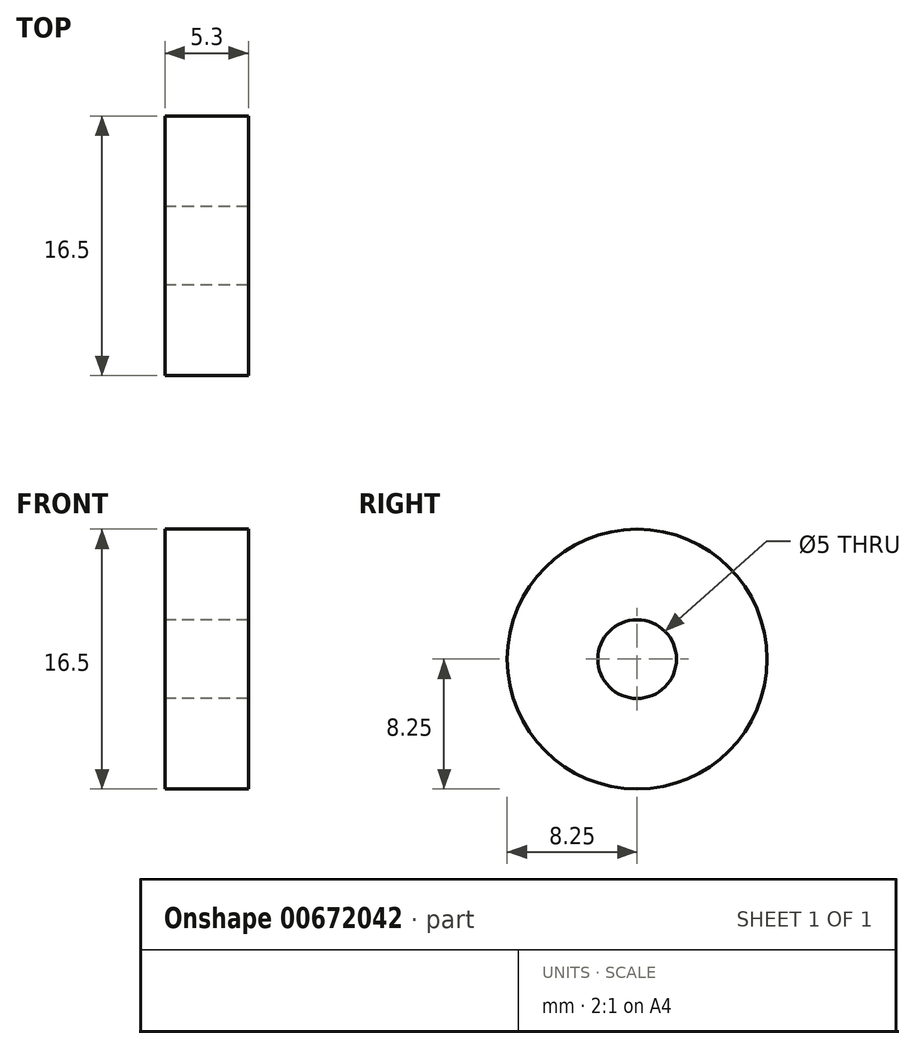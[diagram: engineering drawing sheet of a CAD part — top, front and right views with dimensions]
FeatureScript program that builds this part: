
annotation { "Feature Type Name" : "Feature", "Feature Type Description" : "" }
export const myFeature = defineFeature(function(context is Context, id is Id, definition is map)
    precondition{}
    {
        {
            var Q0;
            Q0=qCreatedBy(makeId("Right.planeOp"),FACE);
            var sketch = newSketch(context, id + "F0", { "sketchPlane" : qUnion([Q0])});
            skCircle(sketch, "E0", {"center": v(0, 0) * mm, "radius": 2.5 * mm});
            skCircle(sketch, "E1", {"center": v(0, 0) * mm, "radius": 8.25 * mm});
            skSolve(sketch);
        }
        {
            var Q0;
            Q0=makeQuery(id+"F0.imprint","IMPRINT",FACE,{"disambiguationData":[TD([[makeQuery(id+"F0.imprint","IMPRINT",EDGE,{"derivedFrom":sQuery(id+"F0.wireOp",EDGE,"E0")}),-1.0]])]});
            extrude(context, id + "F1", {"entities" : qUnion([Q0]), "endBound" : BoundingType.SYMMETRIC, "depth" : 5.3 * mm, "offsetDistance" : 25 * mm});
        }
    });
